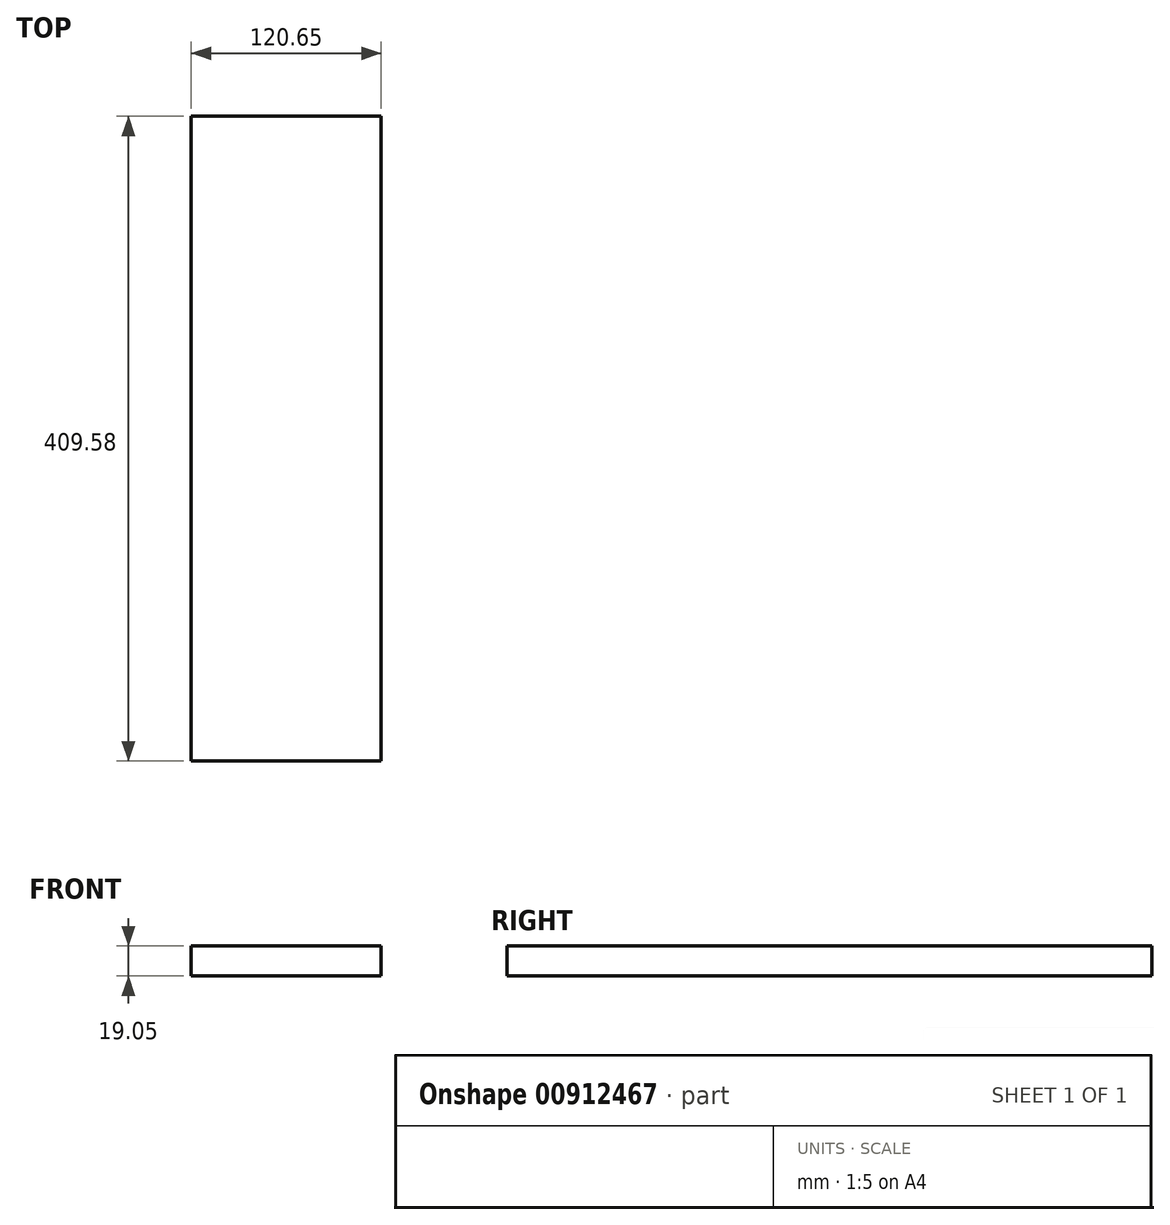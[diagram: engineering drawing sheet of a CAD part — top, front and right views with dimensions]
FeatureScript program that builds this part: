
annotation { "Feature Type Name" : "Feature", "Feature Type Description" : "" }
export const myFeature = defineFeature(function(context is Context, id is Id, definition is map)
    precondition{}
    {
        {
            var Q0;
            Q0=qCreatedBy(makeId("Front.planeOp"),FACE);
            var sketch = newSketch(context, id + "F0", { "sketchPlane" : qUnion([Q0])});
            skLineSegment(sketch, "E0.bottom", {"start": v(0, 0) * mm, "end": v(120.65, 0) * mm});
            skLineSegment(sketch, "E0.top", {"start": v(0, 19.05) * mm, "end": v(120.65, 19.05) * mm});
            skLineSegment(sketch, "E0.left", {"start": v(0, 0) * mm, "end": v(0, 19.05) * mm});
            skLineSegment(sketch, "E0.right", {"start": v(120.65, 0) * mm, "end": v(120.65, 19.05) * mm});
            skSolve(sketch);
        }
        {
            var Q0;
            Q0 = qSketchRegion(id + "F0", true);
            extrude(context, id + "F1", {"entities" : qUnion([Q0]), "depth" : 409.57 * mm, "offsetDistance" : 25.4 * mm});
        }
    });
